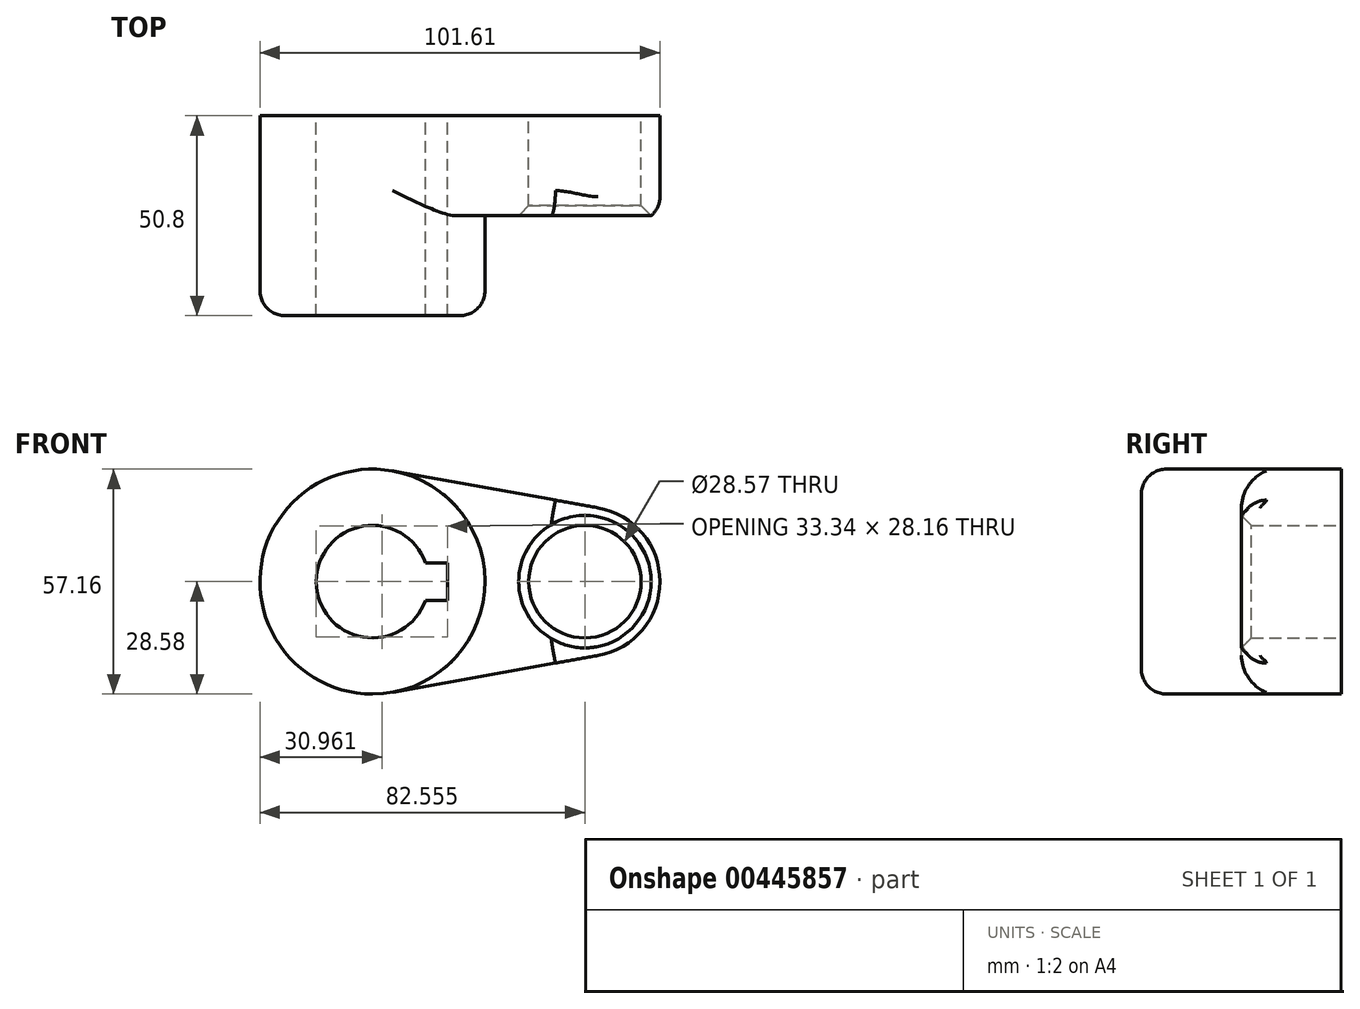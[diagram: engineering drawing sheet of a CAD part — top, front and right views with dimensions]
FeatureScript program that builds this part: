
annotation { "Feature Type Name" : "Feature", "Feature Type Description" : "" }
export const myFeature = defineFeature(function(context is Context, id is Id, definition is map)
    precondition{}
    {
        {
            var Q0;
            Q0=qCreatedBy(makeId("Front.planeOp"),FACE);
            var sketch = newSketch(context, id + "F0", { "sketchPlane" : qUnion([Q0])});
            skCircle(sketch, "E0", {"center": v(0, 0) * mm, "radius": 28.58 * mm});
            skCircle(sketch, "E1", {"center": v(53.98, 0) * mm, "radius": 19.05 * mm});
            skLineSegment(sketch, "E2", {"start": v(5.04, 28.13) * mm, "end": v(57.34, 18.75) * mm});
            skLineSegment(sketch, "E3", {"start": v(5.04, -28.13) * mm, "end": v(57.34, -18.75) * mm});
            skCircle(sketch, "E4", {"center": v(0, 0) * mm, "radius": 14.29 * mm});
            skCircle(sketch, "E5", {"center": v(53.98, 0) * mm, "radius": 14.29 * mm});
            skLineSegment(sketch, "E6.bottom", {"start": v(19.05, 4.76) * mm, "end": v(-19.05, 4.76) * mm});
            skLineSegment(sketch, "E6.top", {"start": v(19.05, -4.76) * mm, "end": v(-19.05, -4.76) * mm});
            skLineSegment(sketch, "E6.left", {"start": v(19.05, 4.76) * mm, "end": v(19.05, -4.76) * mm});
            skLineSegment(sketch, "E6.right", {"start": v(-19.05, 4.76) * mm, "end": v(-19.05, -4.76) * mm});
            skSolve(sketch);
        }
        {
            var Q0;
            {var subQ7=sQuery(id+"F0.wireOp",EDGE,"E6.left");Q0=makeQuery(id+"F0.imprint","IMPRINT",FACE,{"disambiguationData":[TD([[makeQuery(id+"F0.imprint","IMPRINT",EDGE,{"derivedFrom":subQ7}),1.0]])]});}
            var Q1;
            {var subQ0=sQuery(id+"F0.wireOp",EDGE,"E2");Q1=makeQuery(id+"F0.imprint","IMPRINT",FACE,{"disambiguationData":[TD([[makeQuery(id+"F0.imprint","IMPRINT",EDGE,{"derivedFrom":subQ0}),-1.0]])]});}
            var Q2;
            Q2=makeQuery(id+"F0.imprint","IMPRINT",FACE,{"disambiguationData":[TD([[makeQuery(id+"F0.imprint","IMPRINT",EDGE,{"derivedFrom":sQuery(id+"F0.wireOp",EDGE,"E5")}),-1.0]])]});
            var Q3;
            {var subQ5=sQuery(id+"F0.wireOp",EDGE,"E6.right");Q3=makeQuery(id+"F0.imprint","IMPRINT",FACE,{"disambiguationData":[TD([[makeQuery(id+"F0.imprint","IMPRINT",EDGE,{"derivedFrom":subQ5}),1.0]])]});}
            extrude(context, id + "F1", {"entities" : qUnion([Q0, Q1, Q2, Q3]), "depth" : 25.4 * mm});
        }
        {
            var Q0;
            {var subQ7=sQuery(id+"F0.wireOp",EDGE,"E6.left");Q0=makeQuery(id+"F0.imprint","IMPRINT",FACE,{"disambiguationData":[TD([[makeQuery(id+"F0.imprint","IMPRINT",EDGE,{"derivedFrom":subQ7}),1.0]])]});}
            var Q1;
            {var subQ5=sQuery(id+"F0.wireOp",EDGE,"E6.right");Q1=makeQuery(id+"F0.imprint","IMPRINT",FACE,{"disambiguationData":[TD([[makeQuery(id+"F0.imprint","IMPRINT",EDGE,{"derivedFrom":subQ5}),1.0]])]});}
            extrude(context, id + "F2", {"entities" : qUnion([Q0, Q1]), "operationType" : NewBodyOperationType.ADD, "depth" : 50.8 * mm});
        }
        {
            var Q0;
            Q0=makeQuery(id+"F2.opExtrude","CAP_EDGE",EDGE,{"disambiguationData":[OSD([sQuery(id+"F0.wireOp",EDGE,"E0")])],"isStart":false});
            fillet(context, id + "F3", {"entities" : qUnion([Q0]), "radius" : 6.35 * mm, "tangentPropagation" : true, "allowEdgeOverflow" : false});
        }
        {
            var Q0;
            Q0=makeQuery(id+"F1.opExtrude","CAP_EDGE",EDGE,{"disambiguationData":[OSD([sQuery(id+"F0.wireOp",EDGE,"E5")])],"isStart":false});
            chamfer(context, id + "F4", {"entities" : qUnion([Q0]), "width" : 2.54 * mm, "tangentPropagation" : true});
        }
        {
            var Q0;
            Q0=makeQuery(id+"F1.opExtrude","CAP_EDGE",EDGE,{"disambiguationData":[OSD([sQuery(id+"F0.wireOp",EDGE,"E3")])],"isStart":false});
            var Q1;
            Q1=makeQuery(id+"F1.opExtrude","CAP_EDGE",EDGE,{"disambiguationData":[OSD([sQuery(id+"F0.wireOp",EDGE,"E2")])],"isStart":false});
            fillet(context, id + "F5", {"entities" : qUnion([Q0, Q1]), "radius" : 6.35 * mm, "tangentPropagation" : true, "allowEdgeOverflow" : false});
        }
    });
